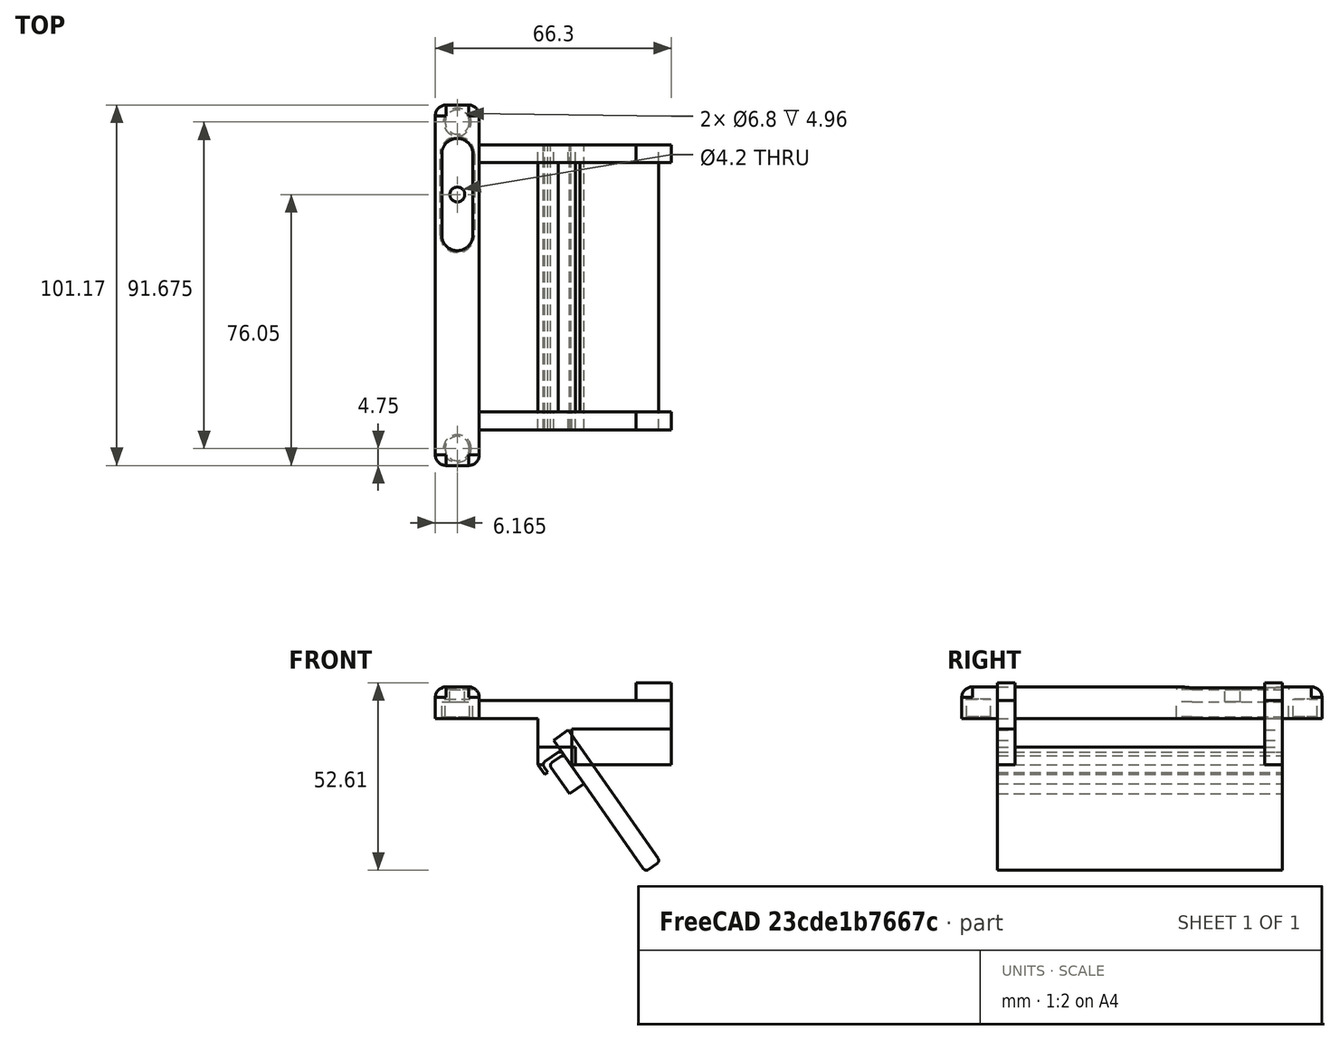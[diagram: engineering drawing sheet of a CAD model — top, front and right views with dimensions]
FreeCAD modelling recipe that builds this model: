
FCSTD DOCUMENT  (FreeCAD 1.0R39109 (Git))
Label: launch-stand-v3
License: All rights reserved
LicenseURL: https://en.wikipedia.org/wiki/All_rights_reserved
objects: Part::Box×22, Part::Cut×11, Part::Fillet×8, App::DocumentObjectGroup×4, Part::MultiFuse×3, Part::Feature×1
note: 45 computed .brp shape members not serialized (recipe doc carries the construction recipe); baked Part::Feature solids carry a one-line shape summary decoded from their .brp

FEATURE [Part::Feature] Part__Feature  label="PN-000336 v7"
  shape: bbox 12.33 x 101.2 x 8.862 mm, 40 faces (baked)
FEATURE [Part::Box] Box  label="Cube"
  AttacherType = Attacher::AttachEngine3D
  Height = 5
  Length = 54
  Placement = pos=(12.3,10,0) rot=(0,0,1;0rad)
  Width = 5
FEATURE [Part::Box] Box001  label="Cube001"
  AttacherType = Attacher::AttachEngine3D
  Height = 13
  Length = 44
  Placement = pos=(22.3,10,-13) rot=(0,0,1;0rad)
  Width = 5
FEATURE [Part::Box] Box002  label="Cube002"
  AttacherType = Attacher::AttachEngine3D
  Height = 5
  Length = 54
  Placement = pos=(12.3,85,0) rot=(0,0,1;0rad)
  Width = 5
FEATURE [Part::Box] Box003  label="Cube003"
  AttacherType = Attacher::AttachEngine3D
  Height = 13
  Length = 44
  Placement = pos=(22.3,85,-13) rot=(0,0,1;0rad)
  Width = 5
FEATURE [Part::Box] Box004  label="Cube004"
  AttacherType = Attacher::AttachEngine3D
  Height = 45
  Length = 5
  Placement = pos=(59,10,-43) rot=(0,1,0;-0.610865rad)
  Width = 80
FEATURE [Part::Box] Box005  label="Cube005"
  AttacherType = Attacher::AttachEngine3D
  Height = 6.25
  Length = 3
  Placement = pos=(32.3,10,-18) rot=(0,1,0;-0.610865rad)
  Width = 80
FEATURE [Part::Box] Box006  label="Cube006"
  AttacherType = Attacher::AttachEngine3D
  Height = 5
  Length = 17
  Placement = pos=(22.3,10,-13) rot=(0,0,1;0rad)
  Width = 80
FEATURE [Part::Box] Box007  label="Cube007"
  AttacherType = Attacher::AttachEngine3D
  Height = 5
  Length = 10
  Placement = pos=(31.9,10,-13) rot=(0,1,0;0.959931rad)
  Width = 80
FEATURE [Part::Fillet] Fillet
  Base = -> Box007
  EdgeLinks = -> Box007 [Edge2,Edge4]
  Edges = 2 edges r=1: [Edge2,Edge4]
FEATURE [Part::MultiFuse] Fusion
  Shapes = -> [Box,Box001]
FEATURE [Part::MultiFuse] Fusion001
  Shapes = -> [Box002,Box003]
FEATURE [Part::Box] Box008  label="Cube008"
  AttacherType = Attacher::AttachEngine3D
  Height = 5
  Length = 10
  Placement = pos=(31.9,10,-13) rot=(0,1,0;0.959931rad)
  Width = 80
FEATURE [Part::Fillet] Fillet001
  Base = -> Box008
  EdgeLinks = -> Box008 [Edge2,Edge4]
  Edges = 2 edges r=1: [Edge2,Edge4]
FEATURE [Part::Box] Box009  label="Cube009"
  AttacherType = Attacher::AttachEngine3D
  Height = 5
  Length = 10
  Placement = pos=(31.9,10,-13) rot=(0,1,0;0.959931rad)
  Width = 80
FEATURE [Part::Fillet] Fillet002
  Base = -> Box009
  EdgeLinks = -> Box009 [Edge2,Edge4]
  Edges = 2 edges r=1: [Edge2,Edge4]
FEATURE [Part::Cut] Cut
  Base = -> Fusion
  Tool = -> Fillet
FEATURE [Part::Cut] Cut001
  Base = -> Fusion001
  Tool = -> Fillet001
FEATURE [Part::Box] Box010  label="Cube010"
  AttacherType = Attacher::AttachEngine3D
  Height = 5
  Length = 10
  Placement = pos=(31.9,10,-13) rot=(0,1,0;0.959931rad)
  Width = 80
FEATURE [Part::Fillet] Fillet003
  Base = -> Box010
  EdgeLinks = -> Box010 [Edge2,Edge4]
  Edges = 2 edges r=1: [Edge2,Edge4]
FEATURE [Part::MultiFuse] Fusion002
  Shapes = -> [Box006,Box005]
FEATURE [Part::Cut] Cut002
  Base = -> Fusion002
  Tool = -> Fillet002
FEATURE [Part::Box] Box011  label="Cube011"
  AttacherType = Attacher::AttachEngine3D
  Height = 8
  Length = 26
  Placement = pos=(22.3,15,-8) rot=(0,0,1;0rad)
  Width = 70
FEATURE [Part::Cut] Cut003
  Base = -> Box004
  Tool = -> Box011
FEATURE [Part::Fillet] Fillet004
  Base = -> Cut003
  EdgeLinks = -> Cut003 [Edge7,Edge22]
  Edges = 2 edges r=1: [Edge7,Edge22]
FEATURE [Part::Box] Box012  label="Cube012"
  AttacherType = Attacher::AttachEngine3D
  Height = 5
  Length = 10
  Placement = pos=(56.3,10,5) rot=(0,0,1;0rad)
  Width = 5
FEATURE [Part::Box] Box013  label="Cube013"
  AttacherType = Attacher::AttachEngine3D
  Height = 5
  Length = 10
  Placement = pos=(56.3,85,5) rot=(0,0,1;0rad)
  Width = 5
FEATURE [Part::Box] Box014  label="Cube014"
  AttacherType = Attacher::AttachEngine3D
  Height = 13
  Length = 6.5
  Placement = pos=(22.3,10,-13) rot=(0,0,1;0rad)
  Width = 80
FEATURE [App::DocumentObjectGroup] Group003  label="Feet"
  Group = -> [Box012,Box013]
FEATURE [Part::Box] Box015  label="Cube015"
  AttacherType = Attacher::AttachEngine3D
  Height = 13
  Length = 6.5
  Placement = pos=(22.3,10,-13) rot=(0,0,1;0rad)
  Width = 80
FEATURE [Part::Box] Box016  label="Cube016"
  AttacherType = Attacher::AttachEngine3D
  Height = 13
  Length = 6.5
  Placement = pos=(22.3,10,-13) rot=(0,0,1;0rad)
  Width = 80
FEATURE [Part::Cut] Cut004
  Base = -> Cut001
  Tool = -> Box014
FEATURE [Part::Cut] Cut005
  Base = -> Cut
  Tool = -> Box015
FEATURE [Part::Cut] Cut006
  Base = -> Cut002
  Tool = -> Box016
FEATURE [Part::Box] Box017  label="Cube017"
  AttacherType = Attacher::AttachEngine3D
  Height = 10
  Length = 28
  Placement = pos=(38.3,10,-13) rot=(0,0,1;0rad)
  Width = 5
FEATURE [Part::Box] Box018  label="Cube018"
  AttacherType = Attacher::AttachEngine3D
  Height = 6.5
  Length = 11
  Placement = pos=(29.9,10,-12.75) rot=(0,1,0;0.959931rad)
  Width = 80
FEATURE [Part::Fillet] Fillet005
  Base = -> Box018
  EdgeLinks = -> Box018 [Edge2,Edge4]
  Edges = 2 edges r=1: [Edge2,Edge4]
FEATURE [Part::Box] Box019  label="Cube019"
  AttacherType = Attacher::AttachEngine3D
  Height = 6.5
  Length = 11
  Placement = pos=(29.9,10,-12.75) rot=(0,1,0;0.959931rad)
  Width = 80
FEATURE [Part::Fillet] Fillet006
  Base = -> Box019
  EdgeLinks = -> Box019 [Edge2,Edge4]
  Edges = 2 edges r=1: [Edge2,Edge4]
FEATURE [Part::Cut] Cut007
  Base = -> Cut006
  Tool = -> Fillet005
FEATURE [Part::Box] Box020  label="Cube020"
  AttacherType = Attacher::AttachEngine3D
  Height = 6.5
  Length = 11
  Placement = pos=(29.9,10,-12.75) rot=(0,1,0;0.959931rad)
  Width = 80
FEATURE [Part::Fillet] Fillet007
  Base = -> Box020
  EdgeLinks = -> Box020 [Edge2,Edge4]
  Edges = 2 edges r=1: [Edge2,Edge4]
FEATURE [Part::Cut] Cut008
  Base = -> Cut004
  Tool = -> Fillet006
FEATURE [App::DocumentObjectGroup] Group002  label="Right Side"
  Group = -> [Cut008]
FEATURE [Part::Cut] Cut009
  Base = -> Cut005
  Tool = -> Fillet007
FEATURE [App::DocumentObjectGroup] Group001  label="Left Side"
  Group = -> [Cut009]
FEATURE [App::DocumentObjectGroup] Group  label="Legs"
  Group = -> [Group002,Group001,Group003]
FEATURE [Part::Box] Box021  label="Cube021"
  AttacherType = Attacher::AttachEngine3D
  Height = 10
  Length = 10
  Placement = pos=(26,0,-19) rot=(0,1,0;0.959931rad)
  Width = 101
FEATURE [Part::Cut] Cut010
  Base = -> Cut007
  Tool = -> Box021
